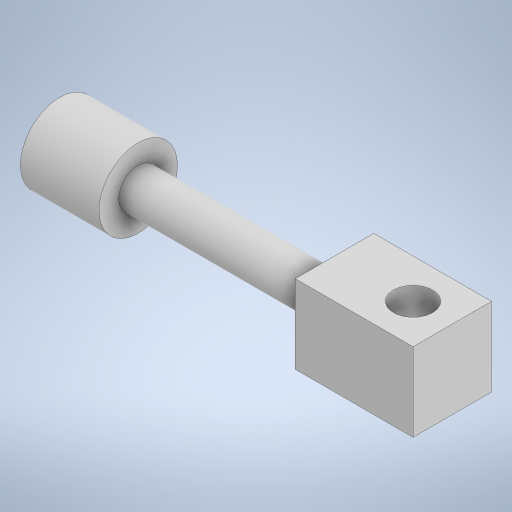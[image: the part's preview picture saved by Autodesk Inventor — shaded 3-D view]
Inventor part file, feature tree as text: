
AUTODESK INVENTOR PART (.ipt)
format: ipt  version: 2023 (Build 270158000, 158)  size: 259,584 bytes
history: native  units: in
note: dims shown in document units (in); Inventor stores cm internally (conversion verified against a paired STEP export)
features: extrude x1, plane x1, revolve x1, sketch x1
ambient origin geometry x8: Origin, YZ Plane, XZ Plane, XY Plane, X Axis, Y Axis, Z Axis, Center Point
bodies: Solid1 (feature_tree)
feature tree (4):
  extrude  "Extrusion1"  Depth=0.5in TaperAngle=0.0deg
  plane  "Work Plane2"
  revolve  "Revolution2"  [1 undecoded]
  sketch  "Sketch4"  dims[d6=0.0in d12=0.5in d13=0.0in d15=0.25in d16=0.25in d17=0.5in d18=0.75in d19=0.25in d20=1.25in d21=0.125in d22=0.25in d23=0.5in d24=360.0deg]
note: 1 required parameter value undecoded (feature->parameter linkage not recoverable at this tier; creation-order binding heuristic only, values carry confidence <= 0.55)
